# Revit family: Workstation-Teknion-Expansion_Casegoods_Private_07-R2013
name_source: partatom
category: Furniture Systems
revit_build: Autodesk Revit Architecture 2014 (Build: 20131024_2115(x64)
units: mm (PartAtom-declared; Revit-internal decimal feet)

## types (1)
- 84" x 96"
    Assembly Code = E2020200
    Depth = 83 5/8"
    Description = 7’ x 8’ workstation
    Exposed Plastic Back Note = Outer Back Finish only applies to the Exposed Plastic Back product options
    Height = 65 5/32"
    Manufacturer = Teknion
    Manufacturer Fax = 416.661.4586
    Model = Expansion Casegoods - Private 07
    Product Line = Expansion Casegoods
    Product Page URL = http://teknionplanningtool.com
    Single Upholstered Note = Same fabric to be applied to seat and inside back
    Sustainability Data = http://www.teknion.com
    URL = http://www.teknion.com
    Unit Weight URL = http://www.teknion.com
    Warranty = http://www.teknion.com
    Width = 95 5/8"

## geometry (parser evidence)
native form markers: Blend x50, Sweep x10
no freeform markers — native parametric forms only
